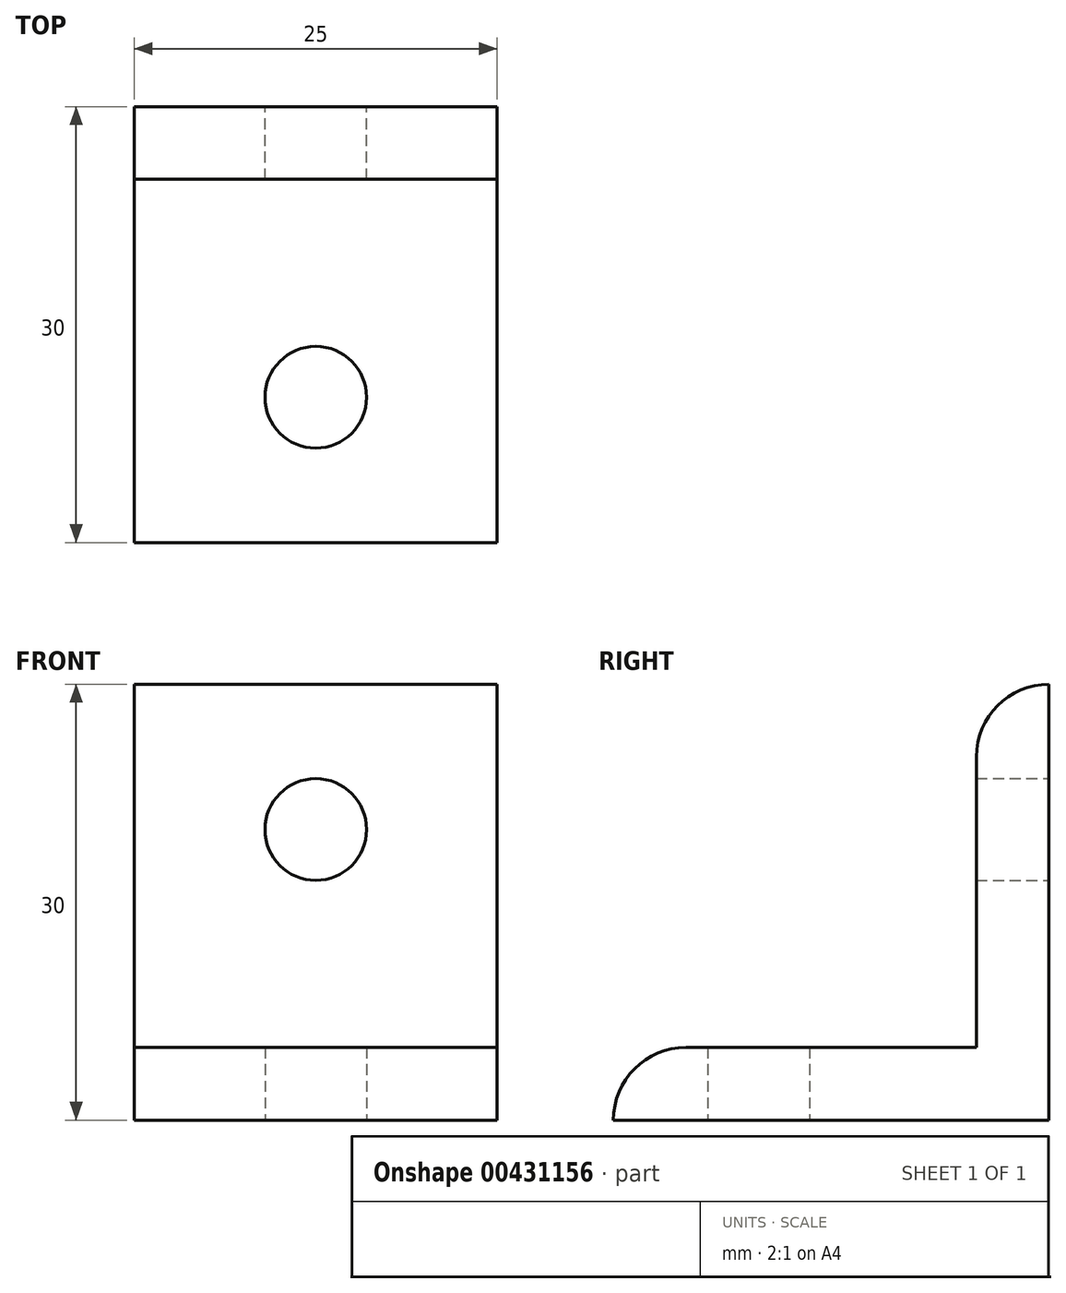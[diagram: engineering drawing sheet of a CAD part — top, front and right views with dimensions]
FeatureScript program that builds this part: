
annotation { "Feature Type Name" : "Feature", "Feature Type Description" : "" }
export const myFeature = defineFeature(function(context is Context, id is Id, definition is map)
    precondition{}
    {
        {
            var Q0;
            Q0=qCreatedBy(makeId("Top.planeOp"),FACE);
            var sketch = newSketch(context, id + "F0", { "sketchPlane" : qUnion([Q0])});
            skLineSegment(sketch, "E0.bottom", {"start": v(12.5, 15) * mm, "end": v(-12.5, 15) * mm});
            skLineSegment(sketch, "E0.top", {"start": v(12.5, -15) * mm, "end": v(-12.5, -15) * mm});
            skLineSegment(sketch, "E0.left", {"start": v(12.5, 15) * mm, "end": v(12.5, -15) * mm});
            skLineSegment(sketch, "E0.right", {"start": v(-12.5, 15) * mm, "end": v(-12.5, -15) * mm});
            skPoint(sketch, "E0.middle", {"position": v(0, 0) * mm});
            skLineSegment(sketch, "E1", {"start": v(0, 15) * mm, "end": v(0, -15) * mm, "construction": true});
            skCircle(sketch, "E2", {"center": v(0, -5) * mm, "radius": 3.5 * mm});
            skLineSegment(sketch, "E3", {"start": v(-12.5, 10) * mm, "end": v(12.5, 10) * mm});
            skSolve(sketch);
        }
        {
            var Q0;
            {var subQ1=sQuery(id+"F0.wireOp",EDGE,"E0.top");Q0=makeQuery(id+"F0.imprint","IMPRINT",FACE,{"disambiguationData":[TD([[makeQuery(id+"F0.imprint","IMPRINT",EDGE,{"derivedFrom":subQ1}),-1.0]])]});}
            extrude(context, id + "F1", {"entities" : qUnion([Q0]), "depth" : 5 * mm});
        }
        {
            var Q0;
            {var subQ0=sQuery(id+"F0.wireOp",EDGE,"E0.bottom");Q0=makeQuery(id+"F0.imprint","IMPRINT",FACE,{"disambiguationData":[TD([[makeQuery(id+"F0.imprint","IMPRINT",EDGE,{"derivedFrom":subQ0}),1.0]])]});}
            extrude(context, id + "F2", {"entities" : qUnion([Q0]), "operationType" : NewBodyOperationType.ADD, "depth" : 30 * mm});
        }
        {
            var Q0;
            Q0=makeQuery(id+"F2.opExtrude","SWEPT_FACE",FACE,{"disambiguationData":[OSD([sQuery(id+"F0.wireOp",EDGE,"E0.bottom")])]});
            var sketch = newSketch(context, id + "F3", { "sketchPlane" : qUnion([Q0])});
            skCircle(sketch, "E4", {"center": v(0, 20) * mm, "radius": 3.5 * mm});
            skSolve(sketch);
        }
        {
            var Q0;
            Q0=makeQuery(id+"F3.imprint","IMPRINT",FACE,{"disambiguationData":[TD([[makeQuery(id+"F3.imprint","IMPRINT",EDGE,{"derivedFrom":sQuery(id+"F3.wireOp",EDGE,"E4")}),1.0]])]});
            extrude(context, id + "F4", {"entities" : qUnion([Q0]), "operationType" : NewBodyOperationType.REMOVE, "oppositeDirection" : true, "depth" : 5 * mm});
        }
        {
            var Q0;
            Q0=makeQuery(id+"F2.opExtrude","CAP_EDGE",EDGE,{"disambiguationData":[OSD([sQuery(id+"F0.wireOp",EDGE,"E3")])],"isStart":false});
            fillet(context, id + "F5", {"entities" : qUnion([Q0]), "radius" : 5 * mm, "tangentPropagation" : true, "allowEdgeOverflow" : false});
        }
        {
            var Q0;
            Q0=makeQuery(id+"F1.opExtrude","CAP_EDGE",EDGE,{"disambiguationData":[OSD([sQuery(id+"F0.wireOp",EDGE,"E0.top")])],"isStart":false});
            fillet(context, id + "F6", {"entities" : qUnion([Q0]), "radius" : 5 * mm, "tangentPropagation" : true, "allowEdgeOverflow" : false});
        }
    });
